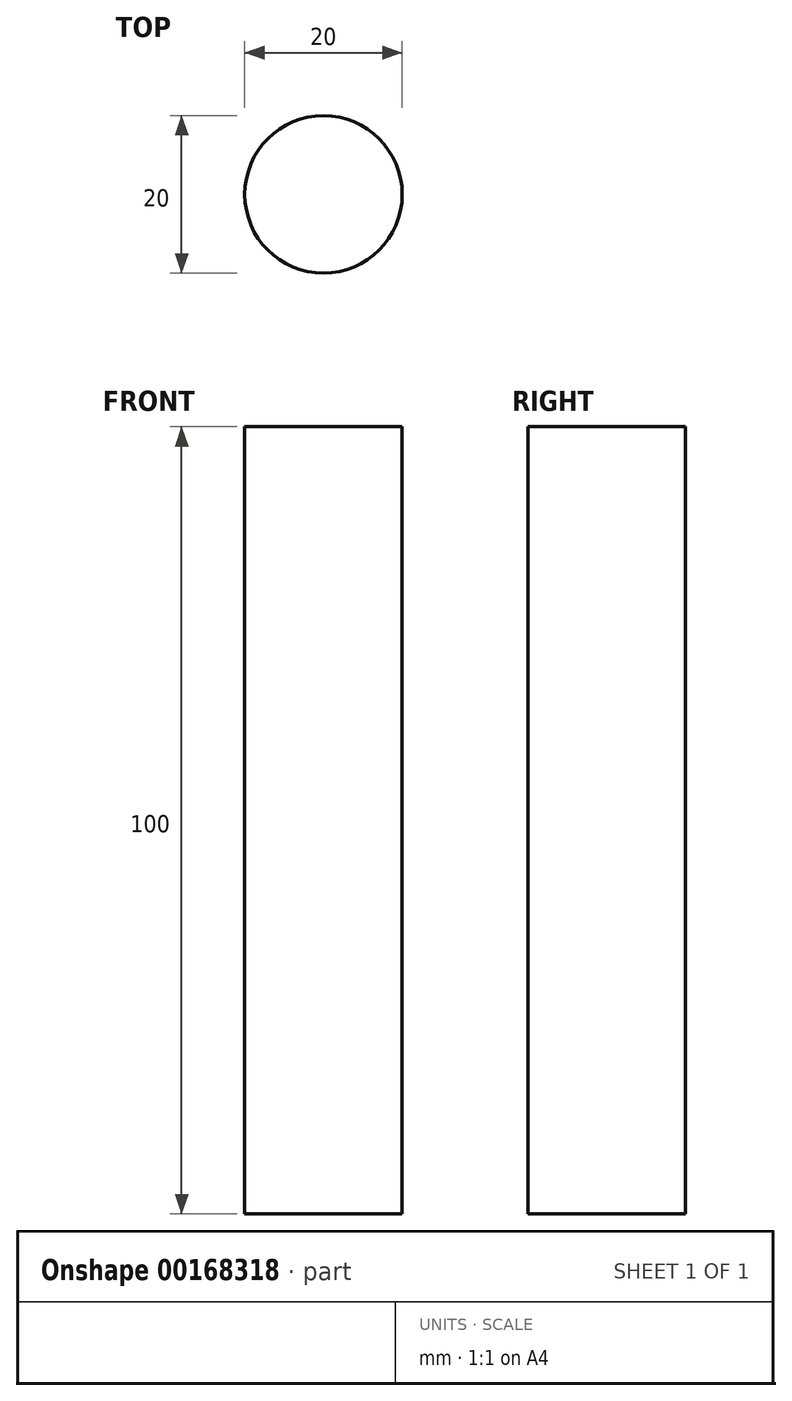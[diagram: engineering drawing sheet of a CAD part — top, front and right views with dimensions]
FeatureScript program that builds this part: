
annotation { "Feature Type Name" : "Feature", "Feature Type Description" : "" }
export const myFeature = defineFeature(function(context is Context, id is Id, definition is map)
    precondition{}
    {
        {
            var Q0;
            Q0=qCreatedBy(makeId("Top.planeOp"),FACE);
            var sketch = newSketch(context, id + "F0", { "sketchPlane" : qUnion([Q0])});
            skCircle(sketch, "E0", {"center": v(0, 0) * mm, "radius": 10 * mm});
            skSolve(sketch);
        }
        {
            var Q0;
            Q0 = qSketchRegion(id + "F0", true);
            extrude(context, id + "F1", {"entities" : qUnion([Q0]), "depth" : 50 * mm});
        }
        {
            var Q0;
            Q0=makeQuery(id+"F1.opExtrude","CAP_FACE",FACE,{"disambiguationData":[OSD([sQuery(id+"F0.wireOp",EDGE,"E0")])],"isStart":true});
            extrude(context, id + "F2", {"entities" : qUnion([Q0]), "operationType" : NewBodyOperationType.ADD, "depth" : 50 * mm});
        }
    });
